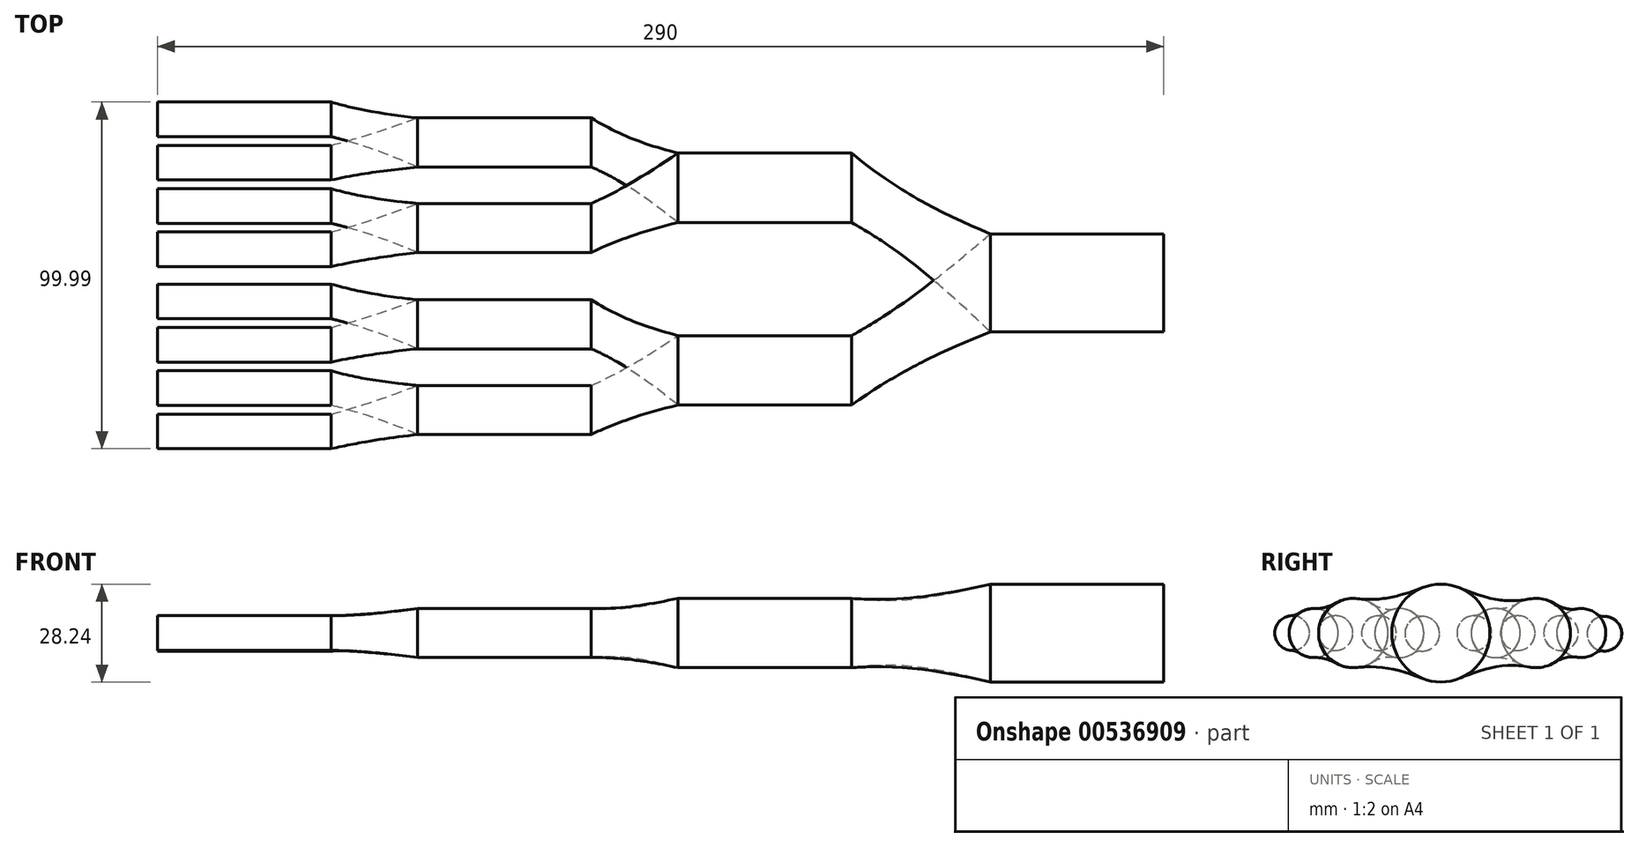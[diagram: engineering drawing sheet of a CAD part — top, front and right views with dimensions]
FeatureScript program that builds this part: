
annotation { "Feature Type Name" : "Feature", "Feature Type Description" : "" }
export const myFeature = defineFeature(function(context is Context, id is Id, definition is map)
    precondition{}
    {
        {
            var Q0;
            Q0=qCreatedBy(makeId("Right.planeOp"),FACE);
            var sketch = newSketch(context, id + "F0", { "sketchPlane" : qUnion([Q0])});
            skCircle(sketch, "E0", {"center": v(-7.5, -0.2) * mm, "radius": 5 * mm});
            skLineSegment(sketch, "E1", {"start": v(-7.5, -0.2) * mm, "end": v(0, 0) * mm, "construction": true});
            skCircle(sketch, "E2", {"center": v(-20, -0.01) * mm, "radius": 5 * mm});
            skLineSegment(sketch, "E3", {"start": v(-20, -0.01) * mm, "end": v(-12.5, -0.01) * mm, "construction": true});
            skCircle(sketch, "E4", {"center": v(-32.5, 0) * mm, "radius": 5 * mm});
            skLineSegment(sketch, "E5", {"start": v(-32.5, 0) * mm, "end": v(-25, 0) * mm, "construction": true});
            skCircle(sketch, "E6", {"center": v(-45, 0) * mm, "radius": 5 * mm});
            skLineSegment(sketch, "E7", {"start": v(-45, 0) * mm, "end": v(-37.5, 0) * mm, "construction": true});
            skCircle(sketch, "E8", {"center": v(45, -0.2) * mm, "radius": 5 * mm});
            skLineSegment(sketch, "E9", {"start": v(45, -0.2) * mm, "end": v(64.04, 0.3) * mm, "construction": true});
            skCircle(sketch, "E10", {"center": v(32.5, -0.01) * mm, "radius": 5 * mm});
            skLineSegment(sketch, "E11", {"start": v(32.5, -0.01) * mm, "end": v(40, -0.01) * mm, "construction": true});
            skCircle(sketch, "E12", {"center": v(20, 0) * mm, "radius": 5 * mm});
            skLineSegment(sketch, "E13", {"start": v(20, 0) * mm, "end": v(27.5, 0) * mm, "construction": true});
            skCircle(sketch, "E14", {"center": v(7.5, 0) * mm, "radius": 5 * mm});
            skLineSegment(sketch, "E15", {"start": v(7.5, 0) * mm, "end": v(15, 0) * mm, "construction": true});
            skLineSegment(sketch, "E16", {"start": v(7.5, 0) * mm, "end": v(0, 0) * mm, "construction": true});
            skSolve(sketch);
        }
        {
            var Q0;
            Q0 = qSketchRegion(id + "F0", true);
            extrude(context, id + "F1", {"entities" : qUnion([Q0]), "depth" : 50 * mm, "offsetDistance" : 25.4 * mm});
        }
        {
            var Q0;
            Q0=makeQuery(id+"F1.opExtrude","CAP_FACE",FACE,{"disambiguationData":[OSD([sQuery(id+"F0.wireOp",EDGE,"E6")])],"isStart":false});
            cPlane(context, id + "F2", {"entities" : qUnion([Q0]), "cplaneType" : CPlaneType.OFFSET, "offset" : 25 * mm, "width" : 150 * mm, "height" : 150 * mm});
        }
        {
            var Q0;
            Q0=qCreatedBy(id+"F2.planeOp",FACE);
            var sketch = newSketch(context, id + "F3", { "sketchPlane" : qUnion([Q0])});
            skCircle(sketch, "E17", {"center": v(-38.8, 0) * mm, "radius": 7.07 * mm});
            skLineSegment(sketch, "E18", {"start": v(0, 0) * mm, "end": v(-71.24, 0) * mm, "construction": true});
            skCircle(sketch, "E19", {"center": v(-14.1, 0) * mm, "radius": 7.07 * mm});
            skCircle(sketch, "E20", {"center": v(13.66, 0) * mm, "radius": 7.07 * mm});
            skCircle(sketch, "E21", {"center": v(38.33, 0) * mm, "radius": 7.07 * mm});
            skSolve(sketch);
        }
        {
            var Q0;
            Q0 = qSketchRegion(id + "F3", true);
            extrude(context, id + "F4", {"entities" : qUnion([Q0]), "depth" : 50 * mm, "offsetDistance" : 25 * mm});
        }
        {
            var Q0;
            Q0=makeQuery(id+"F4.opExtrude","CAP_FACE",FACE,{"disambiguationData":[OSD([sQuery(id+"F3.wireOp",EDGE,"E17")])],"isStart":false});
            cPlane(context, id + "F5", {"entities" : qUnion([Q0]), "cplaneType" : CPlaneType.OFFSET, "offset" : 25 * mm, "width" : 150 * mm, "height" : 150 * mm});
        }
        {
            var Q0;
            Q0=qCreatedBy(id+"F5.planeOp",FACE);
            var sketch = newSketch(context, id + "F6", { "sketchPlane" : qUnion([Q0])});
            skCircle(sketch, "E22", {"center": v(-27.37, 0) * mm, "radius": 10 * mm});
            skCircle(sketch, "E23", {"center": v(25.24, 0) * mm, "radius": 10 * mm});
            skSolve(sketch);
        }
        {
            var Q0;
            Q0 = qSketchRegion(id + "F6", true);
            extrude(context, id + "F7", {"entities" : qUnion([Q0]), "depth" : 50 * mm, "offsetDistance" : 25 * mm});
        }
        {
            var Q0;
            Q0=makeQuery(id+"F7.opExtrude","CAP_FACE",FACE,{"disambiguationData":[OSD([sQuery(id+"F6.wireOp",EDGE,"E22")])],"isStart":false});
            cPlane(context, id + "F8", {"entities" : qUnion([Q0]), "cplaneType" : CPlaneType.OFFSET, "offset" : 40 * mm, "width" : 150 * mm, "height" : 150 * mm});
        }
        {
            var Q0;
            Q0=qCreatedBy(id+"F8.planeOp",FACE);
            var sketch = newSketch(context, id + "F9", { "sketchPlane" : qUnion([Q0])});
            skCircle(sketch, "E24", {"center": v(-2.14, 0) * mm, "radius": 14.12 * mm});
            skSolve(sketch);
        }
        {
            var Q0;
            Q0=makeQuery(id+"F9.imprint","IMPRINT",FACE,{"disambiguationData":[TD([[makeQuery(id+"F9.imprint","IMPRINT",EDGE,{"derivedFrom":sQuery(id+"F9.wireOp",EDGE,"E24")}),1.0]])]});
            extrude(context, id + "F10", {"entities" : qUnion([Q0]), "depth" : 50 * mm, "offsetDistance" : 25 * mm});
        }
        {
            var Q0;
            Q0=makeQuery(id+"F10.opExtrude","CAP_FACE",FACE,{"disambiguationData":[OSD([sQuery(id+"F9.wireOp",EDGE,"E24")])],"isStart":true});
            var Q1;
            Q1=makeQuery(id+"F7.opExtrude","CAP_FACE",FACE,{"disambiguationData":[OSD([sQuery(id+"F6.wireOp",EDGE,"E22")])],"isStart":false});
            loft(context, id + "F11", {"sheetProfilesArray" : [{ "sheetProfileEntities" : qUnion([Q0]) }, { "sheetProfileEntities" : qUnion([Q1]) }]});
        }
        {
            var Q0;
            Q0=makeQuery(id+"F7.opExtrude","CAP_FACE",FACE,{"disambiguationData":[OSD([sQuery(id+"F6.wireOp",EDGE,"E23")])],"isStart":false});
            var Q1;
            Q1=makeQuery(id+"F10.opExtrude","CAP_FACE",FACE,{"disambiguationData":[OSD([sQuery(id+"F9.wireOp",EDGE,"E24")])],"isStart":true});
            loft(context, id + "F12", {"sheetProfilesArray" : [{ "sheetProfileEntities" : qUnion([Q0]) }, { "sheetProfileEntities" : qUnion([Q1]) }]});
        }
        {
            var Q0;
            Q0=makeQuery(id+"F4.opExtrude","CAP_FACE",FACE,{"disambiguationData":[OSD([sQuery(id+"F3.wireOp",EDGE,"E21")])],"isStart":false});
            var Q1;
            Q1=makeQuery(id+"F7.opExtrude","CAP_FACE",FACE,{"disambiguationData":[OSD([sQuery(id+"F6.wireOp",EDGE,"E23")])],"isStart":true});
            loft(context, id + "F13", {"sheetProfilesArray" : [{ "sheetProfileEntities" : qUnion([Q0]) }, { "sheetProfileEntities" : qUnion([Q1]) }]});
        }
        {
            var Q0;
            Q0=makeQuery(id+"F7.opExtrude","CAP_FACE",FACE,{"disambiguationData":[OSD([sQuery(id+"F6.wireOp",EDGE,"E22")])],"isStart":true});
            var Q1;
            Q1=makeQuery(id+"F4.opExtrude","CAP_FACE",FACE,{"disambiguationData":[OSD([sQuery(id+"F3.wireOp",EDGE,"E17")])],"isStart":false});
            loft(context, id + "F14", {"sheetProfilesArray" : [{ "sheetProfileEntities" : qUnion([Q0]) }, { "sheetProfileEntities" : qUnion([Q1]) }]});
        }
        {
            var Q0;
            Q0=makeQuery(id+"F4.opExtrude","CAP_FACE",FACE,{"disambiguationData":[OSD([sQuery(id+"F3.wireOp",EDGE,"E19")])],"isStart":false});
            var Q1;
            Q1=makeQuery(id+"F7.opExtrude","CAP_FACE",FACE,{"disambiguationData":[OSD([sQuery(id+"F6.wireOp",EDGE,"E22")])],"isStart":true});
            loft(context, id + "F15", {"sheetProfilesArray" : [{ "sheetProfileEntities" : qUnion([Q0]) }, { "sheetProfileEntities" : qUnion([Q1]) }]});
        }
        {
            var Q0;
            Q0=makeQuery(id+"F7.opExtrude","CAP_FACE",FACE,{"disambiguationData":[OSD([sQuery(id+"F6.wireOp",EDGE,"E23")])],"isStart":true});
            var Q1;
            Q1=makeQuery(id+"F4.opExtrude","CAP_FACE",FACE,{"disambiguationData":[OSD([sQuery(id+"F3.wireOp",EDGE,"E20")])],"isStart":false});
            loft(context, id + "F16", {"sheetProfilesArray" : [{ "sheetProfileEntities" : qUnion([Q0]) }, { "sheetProfileEntities" : qUnion([Q1]) }]});
        }
        {
            var Q0;
            Q0=makeQuery(id+"F1.opExtrude","CAP_FACE",FACE,{"disambiguationData":[OSD([sQuery(id+"F0.wireOp",EDGE,"E8")])],"isStart":false});
            var Q1;
            Q1=makeQuery(id+"F4.opExtrude","CAP_FACE",FACE,{"disambiguationData":[OSD([sQuery(id+"F3.wireOp",EDGE,"E21")])],"isStart":true});
            loft(context, id + "F17", {"sheetProfilesArray" : [{ "sheetProfileEntities" : qUnion([Q0]) }, { "sheetProfileEntities" : qUnion([Q1]) }]});
        }
        {
            var Q0;
            Q0=makeQuery(id+"F1.opExtrude","CAP_FACE",FACE,{"disambiguationData":[OSD([sQuery(id+"F0.wireOp",EDGE,"E12")])],"isStart":false});
            var Q1;
            Q1=makeQuery(id+"F4.opExtrude","CAP_FACE",FACE,{"disambiguationData":[OSD([sQuery(id+"F3.wireOp",EDGE,"E20")])],"isStart":true});
            loft(context, id + "F18", {"sheetProfilesArray" : [{ "sheetProfileEntities" : qUnion([Q0]) }, { "sheetProfileEntities" : qUnion([Q1]) }]});
        }
        {
            var Q0;
            Q0=makeQuery(id+"F1.opExtrude","CAP_FACE",FACE,{"disambiguationData":[OSD([sQuery(id+"F0.wireOp",EDGE,"E0")])],"isStart":false});
            var Q1;
            Q1=makeQuery(id+"F4.opExtrude","CAP_FACE",FACE,{"disambiguationData":[OSD([sQuery(id+"F3.wireOp",EDGE,"E19")])],"isStart":true});
            loft(context, id + "F19", {"sheetProfilesArray" : [{ "sheetProfileEntities" : qUnion([Q0]) }, { "sheetProfileEntities" : qUnion([Q1]) }]});
        }
        {
            var Q0;
            Q0=makeQuery(id+"F1.opExtrude","CAP_FACE",FACE,{"disambiguationData":[OSD([sQuery(id+"F0.wireOp",EDGE,"E4")])],"isStart":false});
            var Q1;
            Q1=makeQuery(id+"F4.opExtrude","CAP_FACE",FACE,{"disambiguationData":[OSD([sQuery(id+"F3.wireOp",EDGE,"E17")])],"isStart":true});
            loft(context, id + "F20", {"sheetProfilesArray" : [{ "sheetProfileEntities" : qUnion([Q0]) }, { "sheetProfileEntities" : qUnion([Q1]) }]});
        }
        {
            var Q0;
            Q0=makeQuery(id+"F4.opExtrude","CAP_FACE",FACE,{"disambiguationData":[OSD([sQuery(id+"F3.wireOp",EDGE,"E21")])],"isStart":true});
            var Q1;
            Q1=makeQuery(id+"F1.opExtrude","CAP_FACE",FACE,{"disambiguationData":[OSD([sQuery(id+"F0.wireOp",EDGE,"E10")])],"isStart":false});
            loft(context, id + "F21", {"sheetProfilesArray" : [{ "sheetProfileEntities" : qUnion([Q0]) }, { "sheetProfileEntities" : qUnion([Q1]) }]});
        }
        {
            var Q0;
            Q0=makeQuery(id+"F4.opExtrude","CAP_FACE",FACE,{"disambiguationData":[OSD([sQuery(id+"F3.wireOp",EDGE,"E20")])],"isStart":true});
            var Q1;
            Q1=makeQuery(id+"F1.opExtrude","CAP_FACE",FACE,{"disambiguationData":[OSD([sQuery(id+"F0.wireOp",EDGE,"E14")])],"isStart":false});
            loft(context, id + "F22", {"sheetProfilesArray" : [{ "sheetProfileEntities" : qUnion([Q0]) }, { "sheetProfileEntities" : qUnion([Q1]) }]});
        }
        {
            var Q0;
            Q0=makeQuery(id+"F4.opExtrude","CAP_FACE",FACE,{"disambiguationData":[OSD([sQuery(id+"F3.wireOp",EDGE,"E19")])],"isStart":true});
            var Q1;
            Q1=makeQuery(id+"F1.opExtrude","CAP_FACE",FACE,{"disambiguationData":[OSD([sQuery(id+"F0.wireOp",EDGE,"E2")])],"isStart":false});
            loft(context, id + "F23", {"sheetProfilesArray" : [{ "sheetProfileEntities" : qUnion([Q0]) }, { "sheetProfileEntities" : qUnion([Q1]) }]});
        }
        {
            var Q0;
            Q0=makeQuery(id+"F4.opExtrude","CAP_FACE",FACE,{"disambiguationData":[OSD([sQuery(id+"F3.wireOp",EDGE,"E17")])],"isStart":true});
            var Q1;
            Q1=makeQuery(id+"F1.opExtrude","CAP_FACE",FACE,{"disambiguationData":[OSD([sQuery(id+"F0.wireOp",EDGE,"E6")])],"isStart":false});
            loft(context, id + "F24", {"sheetProfilesArray" : [{ "sheetProfileEntities" : qUnion([Q0]) }, { "sheetProfileEntities" : qUnion([Q1]) }]});
        }
    });
